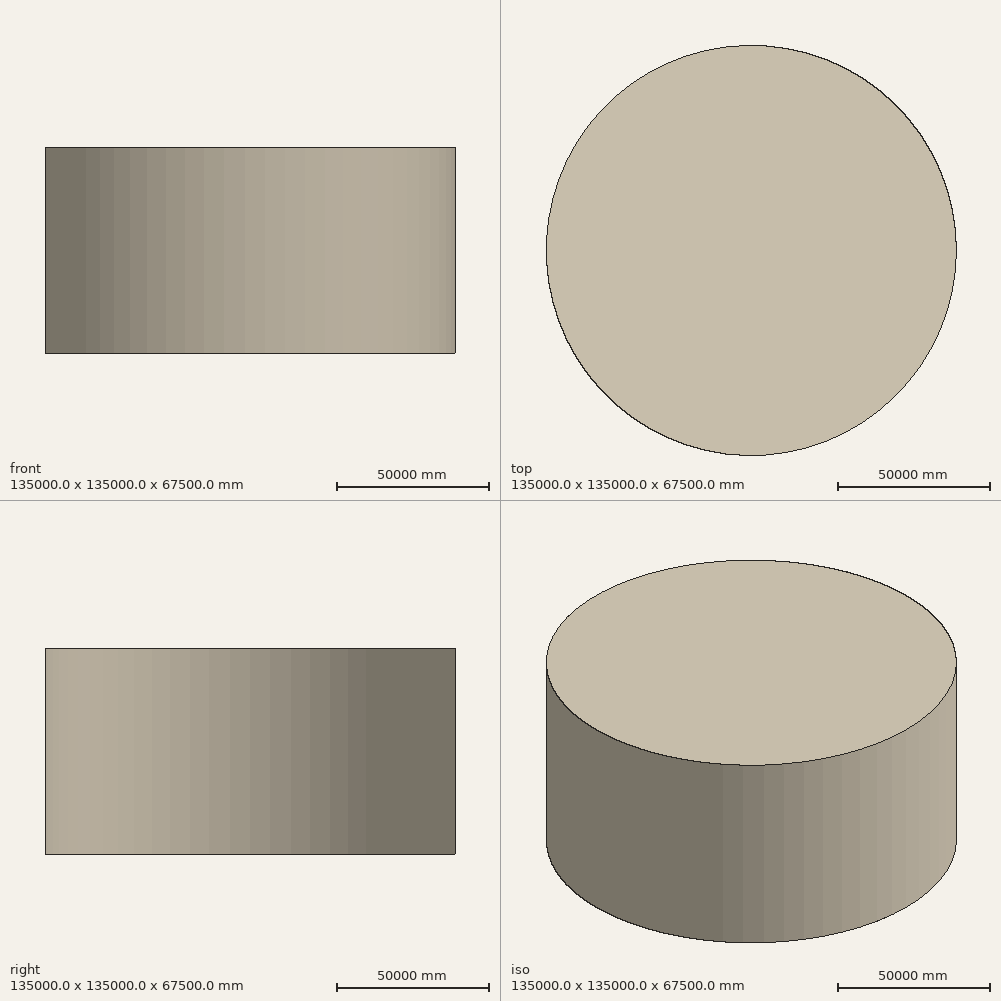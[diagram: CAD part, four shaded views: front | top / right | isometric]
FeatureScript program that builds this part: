
annotation { "Feature Type Name" : "Feature", "Feature Type Description" : "" }
export const myFeature = defineFeature(function(context is Context, id is Id, definition is map)
    precondition{}
    {
        {
            var Q0;
            Q0=qCreatedBy(makeId("Top.planeOp"),FACE);
            var sketch = newSketch(context, id + "F0", { "sketchPlane" : qUnion([Q0])});
            skCircle(sketch, "E0", {"center": v(0, 0) * mm, "radius": 67500 * mm});
            skSolve(sketch);
        }
        {
            var Q0;
            Q0=makeQuery(id+"F0.imprint","IMPRINT",FACE,{"disambiguationData":[TD([[makeQuery(id+"F0.imprint","IMPRINT",EDGE,{"derivedFrom":sQuery(id+"F0.wireOp",EDGE,"E0")}),1.0]])]});
            extrude(context, id + "F1", {"entities" : qUnion([Q0]), "depth" : 67500 * mm, "offsetDistance" : 25 * mm});
        }
    });
